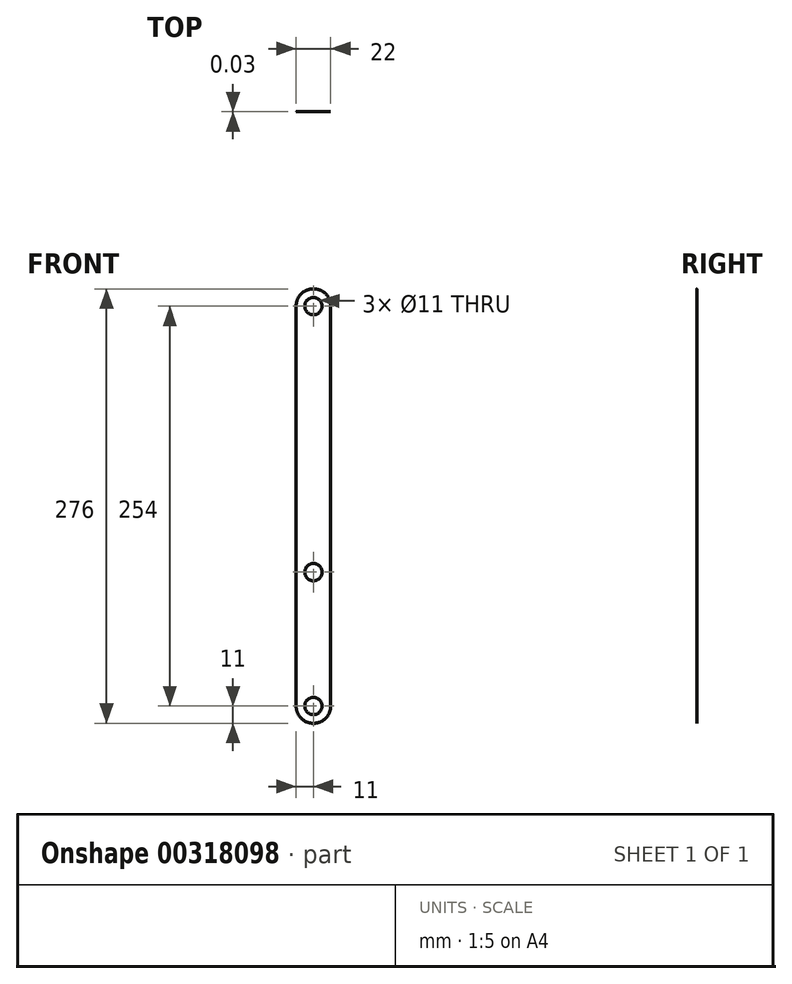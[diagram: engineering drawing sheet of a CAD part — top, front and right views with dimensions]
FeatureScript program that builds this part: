
annotation { "Feature Type Name" : "Feature", "Feature Type Description" : "" }
export const myFeature = defineFeature(function(context is Context, id is Id, definition is map)
    precondition{}
    {
        {
            var Q0;
            Q0=qCreatedBy(makeId("Front.planeOp"),FACE);
            var sketch = newSketch(context, id + "F0", { "sketchPlane" : qUnion([Q0])});
            skLineSegment(sketch, "E0.left", {"start": v(0, 127) * mm, "end": v(0, -127) * mm, "construction": true});
            skPoint(sketch, "E0.middle", {"position": v(0, 0) * mm});
            skCircle(sketch, "E1", {"center": v(0, 127) * mm, "radius": 5.5 * mm});
            skLineSegment(sketch, "E2.right", {"start": v(11, 127) * mm, "end": v(11, -127) * mm});
            skArc(sketch, "E3", {"start": v(11, 127) * mm, "mid": v(7.78, 134.78) * mm, "end": v(0, 138) * mm});
            skArc(sketch, "E4.MirrorCS", {"start": v(-11, 127) * mm, "mid": v(-7.78, 134.78) * mm, "end": v(0, 138) * mm});
            skLineSegment(sketch, "E5.MirrorCS", {"start": v(-11, 127) * mm, "end": v(-11, -127) * mm});
            skCircle(sketch, "E6.MirrorC", {"center": v(0, -127) * mm, "radius": 5.5 * mm});
            skArc(sketch, "E7.MirrorCS", {"start": v(11, -127) * mm, "mid": v(7.78, -134.78) * mm, "end": v(0, -138) * mm});
            skArc(sketch, "E8.MirrorCS", {"start": v(-11, -127) * mm, "mid": v(-7.78, -134.78) * mm, "end": v(0, -138) * mm});
            skCircle(sketch, "E9.MirrorC", {"center": v(0, -42) * mm, "radius": 5.5 * mm});
            skSolve(sketch);
        }
        {
            var Q0;
            Q0=qSketchRegion(id+"F0",true);
            var Q1;
            Q1=makeQuery(id+"F0.imprint","IMPRINT",FACE,{"disambiguationData":[TD([[makeQuery(id+"F0.imprint","IMPRINT",EDGE,{"derivedFrom":sQuery(id+"F0.wireOp",EDGE,"Rl0T1UDf-7hmJ-BMTz-lLm2-DiDhTJpeqPjR")}),-1.0]])]});
            var Q2;
            Q2=makeQuery(id+"F0.imprint","IMPRINT",FACE,{"disambiguationData":[TD([[makeQuery(id+"F0.imprint","IMPRINT",EDGE,{"derivedFrom":sQuery(id+"F0.wireOp",EDGE,"E1")}),-1.0]])]});
            var Q3;
            Q3=makeQuery(id+"F0.imprint","IMPRINT",FACE,{"disambiguationData":[TD([[makeQuery(id+"F0.imprint","IMPRINT",EDGE,{"derivedFrom":sQuery(id+"F0.wireOp",EDGE,"E1")}),1.0]])]});
            var Q4;
            Q4=makeQuery(id+"F0.imprint","IMPRINT",FACE,{"disambiguationData":[TD([[makeQuery(id+"F0.imprint","IMPRINT",EDGE,{"derivedFrom":sQuery(id+"F0.wireOp",EDGE,"d6dac872-9fba-44d0-9cee-73e14386f9762.MirrorC")}),1.0]])]});
            var Q5;
            Q5=makeQuery(id+"F0.imprint","IMPRINT",FACE,{"disambiguationData":[TD([[makeQuery(id+"F0.imprint","IMPRINT",EDGE,{"derivedFrom":sQuery(id+"F0.wireOp",EDGE,"01b89e5f-d94a-4a93-81c0-860f3d0f2b17.MirrorC")}),1.0]])]});
            extrude(context, id + "F1", {"entities" : qUnion([Q0, Q1, Q2, Q3, Q4, Q5]), "depth" : 3 / 101.6 * mm, "offsetDistance" : 25.4 * mm});
        }
        {
            var Q0;
            Q0=makeQuery(id+"F0.imprint","IMPRINT",FACE,{"disambiguationData":[TD([[makeQuery(id+"F0.imprint","IMPRINT",EDGE,{"derivedFrom":sQuery(id+"F0.wireOp",EDGE,"d6dac872-9fba-44d0-9cee-73e14386f9762.MirrorC")}),1.0]])]});
            var Q1;
            Q1=makeQuery(id+"F0.imprint","IMPRINT",FACE,{"disambiguationData":[TD([[makeQuery(id+"F0.imprint","IMPRINT",EDGE,{"derivedFrom":sQuery(id+"F0.wireOp",EDGE,"E1")}),1.0]])]});
            var Q2;
            Q2=makeQuery(id+"F0.imprint","IMPRINT",FACE,{"disambiguationData":[TD([[makeQuery(id+"F0.imprint","IMPRINT",EDGE,{"derivedFrom":sQuery(id+"F0.wireOp",EDGE,"01b89e5f-d94a-4a93-81c0-860f3d0f2b17.MirrorC")}),1.0]])]});
            extrude(context, id + "F2", {"entities" : qUnion([Q0, Q1, Q2]), "operationType" : NewBodyOperationType.REMOVE, "depth" : 1.5 * mm});
        }
    });
